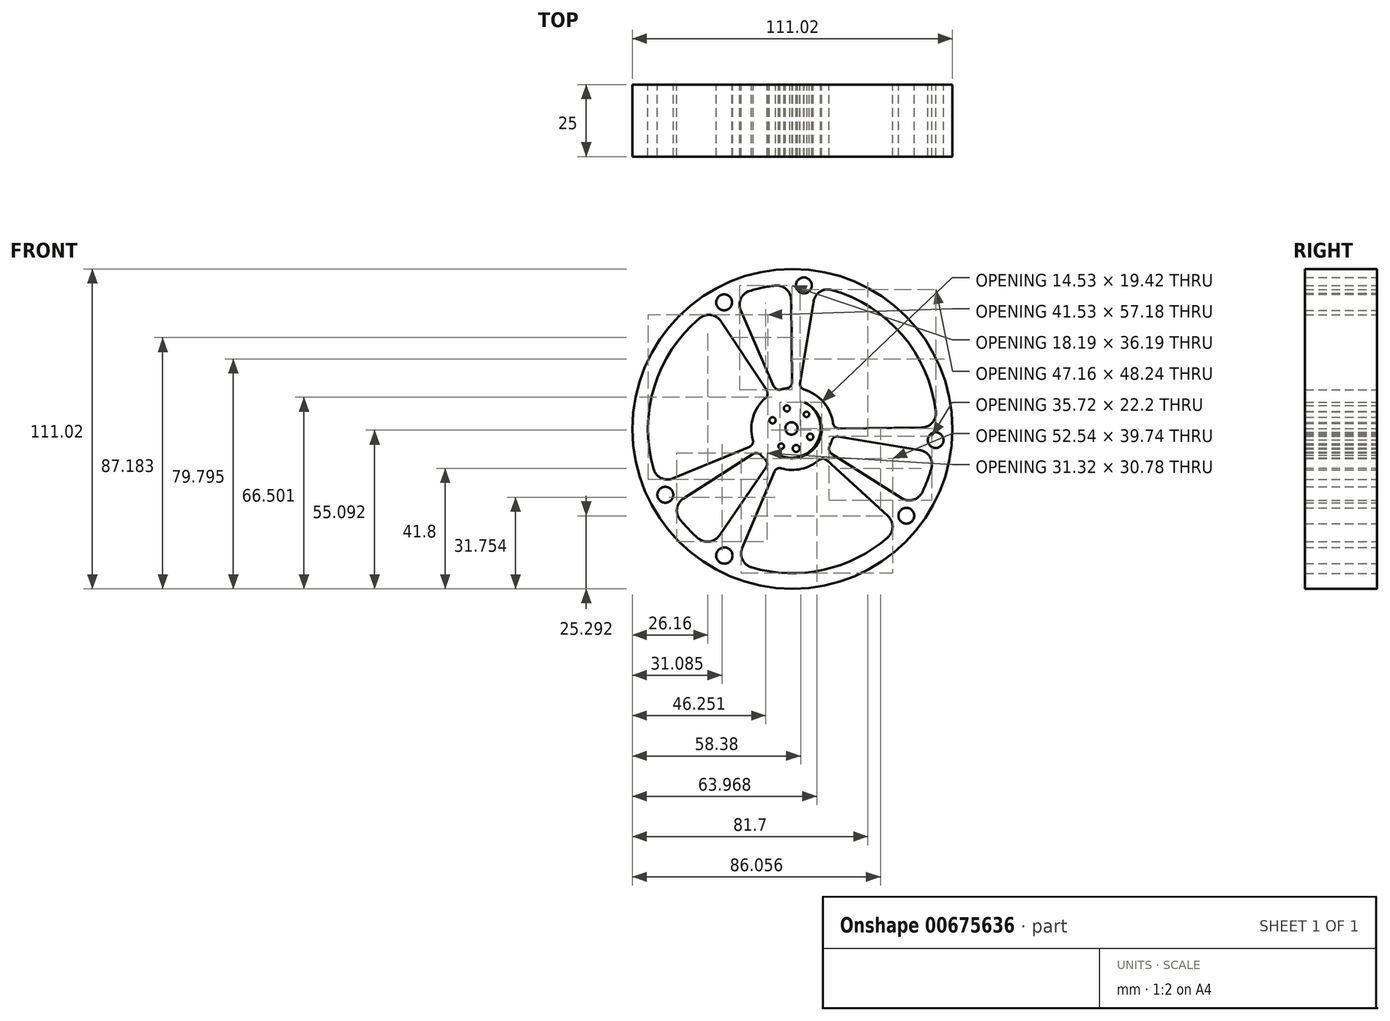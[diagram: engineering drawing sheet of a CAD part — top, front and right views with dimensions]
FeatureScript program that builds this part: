
annotation { "Feature Type Name" : "Feature", "Feature Type Description" : "" }
export const myFeature = defineFeature(function(context is Context, id is Id, definition is map)
    precondition{}
    {
        {
            var Q0;
            Q0=qCreatedBy(makeId("Front.planeOp"),FACE);
            var sketch = newSketch(context, id + "F0", { "sketchPlane" : qUnion([Q0])});
            skArc(sketch, "E0", {"start": v(-6.06, 49.75) * mm, "mid": v(-10.49, 49) * mm, "end": v(-14.83, 47.87) * mm});
            skArc(sketch, "E1", {"start": v(-9.28, 10.8) * mm, "mid": v(-13.63, 4.15) * mm, "end": v(-13.72, -3.8) * mm});
            skLineSegment(sketch, "E2", {"start": v(-0.16, 16.12) * mm, "end": v(-0.45, 44.84) * mm});
            skLineSegment(sketch, "E3", {"start": v(7.34, 44.24) * mm, "end": v(2.64, 15.9) * mm});
            skLineSegment(sketch, "E4", {"start": v(-6.45, 14.77) * mm, "end": v(-17.94, 41.1) * mm});
            skLineSegment(sketch, "E5", {"start": v(-24.8, 37.36) * mm, "end": v(-8.92, 13.43) * mm});
            skLineSegment(sketch, "E6", {"start": v(-14.88, -6.19) * mm, "end": v(-41.4, -17.22) * mm});
            skLineSegment(sketch, "E7", {"start": v(-37.78, -24.15) * mm, "end": v(-13.58, -8.68) * mm});
            skLineSegment(sketch, "E8", {"start": v(-9.11, -13.3) * mm, "end": v(-25.35, -36.99) * mm});
            skLineSegment(sketch, "E9", {"start": v(11.9, -10.87) * mm, "end": v(33.1, -30.25) * mm});
            skLineSegment(sketch, "E10", {"start": v(37.85, -24.04) * mm, "end": v(13.6, -8.64) * mm});
            skLineSegment(sketch, "E11", {"start": v(15.9, -2.64) * mm, "end": v(44.24, -7.34) * mm});
            skLineSegment(sketch, "E12", {"start": v(44.84, 0.45) * mm, "end": v(16.12, 0.16) * mm});
            skLineSegment(sketch, "E13", {"start": v(-17.42, -41.32) * mm, "end": v(-6.26, -14.85) * mm});
            skCircle(sketch, "E14", {"center": v(0, 0) * mm, "radius": 55.5 * mm});
            skArc(sketch, "E15.trimOffspring", {"start": v(49.75, 6.06) * mm, "mid": v(38.07, 32.6) * mm, "end": v(13.63, 48.23) * mm});
            skArc(sketch, "E16.trimOffspring", {"start": v(-14.23, -48.05) * mm, "mid": v(10.73, -48.96) * mm, "end": v(33.02, -37.7) * mm});
            skArc(sketch, "E17.trimOffspring", {"start": v(-38.98, -31.5) * mm, "mid": v(-36, -34.87) * mm, "end": v(-32.74, -37.95) * mm});
            skArc(sketch, "E18.trimOffspring", {"start": v(45.02, -22.02) * mm, "mid": v(46.81, -17.9) * mm, "end": v(48.23, -13.63) * mm});
            skArc(sketch, "E19.trimOffspring", {"start": v(-32.18, 38.43) * mm, "mid": v(-47.95, 14.59) * mm, "end": v(-48.12, -14) * mm});
            skCircle(sketch, "E20", {"center": v(49.69, -3.91) * mm, "radius": 2.7 * mm});
            skCircle(sketch, "E21", {"center": v(39.52, -30.16) * mm, "radius": 2.74 * mm});
            skCircle(sketch, "E22", {"center": v(-23.6, -43.97) * mm, "radius": 2.83 * mm});
            skCircle(sketch, "E23", {"center": v(-44.1, -22.9) * mm, "radius": 2.76 * mm});
            skCircle(sketch, "E24", {"center": v(-23.68, 43.91) * mm, "radius": 2.76 * mm});
            skCircle(sketch, "E25", {"center": v(3.96, 49.82) * mm, "radius": 2.75 * mm});
            skArc(sketch, "E26.trimOffspring", {"start": v(-1.9, 14.12) * mm, "mid": v(-2.98, 13.93) * mm, "end": v(-4.05, 13.66) * mm});
            skArc(sketch, "E27.trimOffspring", {"start": v(14.12, 1.9) * mm, "mid": v(10.82, 9.26) * mm, "end": v(4.04, 13.66) * mm});
            skArc(sketch, "E28.trimOffspring", {"start": v(12.87, -6.1) * mm, "mid": v(13.3, -5.09) * mm, "end": v(13.66, -4.04) * mm});
            skArc(sketch, "E29.trimOffspring", {"start": v(-3.88, -13.7) * mm, "mid": v(3.05, -13.91) * mm, "end": v(9.25, -10.83) * mm});
            skArc(sketch, "E30.trimOffspring", {"start": v(-10.97, -9.09) * mm, "mid": v(-10.23, -9.9) * mm, "end": v(-9.44, -10.67) * mm});
            skPoint(sketch, "E31.visualSharp", {"position": v(-27.72, 41.75) * mm});
            skArc(sketch, "E31.filletArc", {"start": v(-24.8, 37.36) * mm, "mid": v(-28.25, 39.54) * mm, "end": v(-32.18, 38.43) * mm});
            skPoint(sketch, "E32.visualSharp", {"position": v(-46.28, -19.24) * mm});
            skArc(sketch, "E32.filletArc", {"start": v(-48.12, -14) * mm, "mid": v(-45.48, -17.1) * mm, "end": v(-41.4, -17.22) * mm});
            skPoint(sketch, "E33.visualSharp", {"position": v(-20.05, 45.93) * mm});
            skArc(sketch, "E33.filletArc", {"start": v(-14.83, 47.87) * mm, "mid": v(-17.9, 45.18) * mm, "end": v(-17.94, 41.1) * mm});
            skPoint(sketch, "E34.visualSharp", {"position": v(-0.5, 50.12) * mm});
            skArc(sketch, "E34.filletArc", {"start": v(-0.45, 44.84) * mm, "mid": v(-2.16, 48.55) * mm, "end": v(-6.06, 49.75) * mm});
            skPoint(sketch, "E35.visualSharp", {"position": v(8.2, 49.44) * mm});
            skArc(sketch, "E35.filletArc", {"start": v(13.63, 48.23) * mm, "mid": v(9.6, 47.64) * mm, "end": v(7.34, 44.24) * mm});
            skPoint(sketch, "E36.visualSharp", {"position": v(50.12, 0.5) * mm});
            skArc(sketch, "E36.filletArc", {"start": v(44.84, 0.45) * mm, "mid": v(48.55, 2.16) * mm, "end": v(49.75, 6.06) * mm});
            skPoint(sketch, "E37.visualSharp", {"position": v(49.44, -8.2) * mm});
            skArc(sketch, "E37.filletArc", {"start": v(48.23, -13.63) * mm, "mid": v(47.64, -9.6) * mm, "end": v(44.24, -7.34) * mm});
            skPoint(sketch, "E38.visualSharp", {"position": v(42.3, -26.87) * mm});
            skArc(sketch, "E38.filletArc", {"start": v(37.85, -24.04) * mm, "mid": v(41.9, -24.63) * mm, "end": v(45.02, -22.02) * mm});
            skPoint(sketch, "E39.visualSharp", {"position": v(37, -33.8) * mm});
            skArc(sketch, "E39.filletArc", {"start": v(33.02, -37.7) * mm, "mid": v(34.73, -34) * mm, "end": v(33.1, -30.25) * mm});
            skPoint(sketch, "E40.visualSharp", {"position": v(-19.47, -46.18) * mm});
            skArc(sketch, "E40.filletArc", {"start": v(-17.42, -41.32) * mm, "mid": v(-17.33, -45.4) * mm, "end": v(-14.23, -48.05) * mm});
            skPoint(sketch, "E41.visualSharp", {"position": v(-28.33, -41.34) * mm});
            skArc(sketch, "E41.filletArc", {"start": v(-32.74, -37.95) * mm, "mid": v(-28.83, -39.12) * mm, "end": v(-25.35, -36.99) * mm});
            skPoint(sketch, "E42.visualSharp", {"position": v(-42.23, -26.99) * mm});
            skArc(sketch, "E42.filletArc", {"start": v(-37.78, -24.15) * mm, "mid": v(-40.03, -27.56) * mm, "end": v(-38.98, -31.5) * mm});
            skPoint(sketch, "E43.visualSharp", {"position": v(-12, -7.67) * mm});
            skArc(sketch, "E43.filletArc", {"start": v(-10.97, -9.09) * mm, "mid": v(-12.2, -8.39) * mm, "end": v(-13.58, -8.68) * mm});
            skPoint(sketch, "E44.visualSharp", {"position": v(-8.05, -11.75) * mm});
            skArc(sketch, "E44.filletArc", {"start": v(-9.11, -13.3) * mm, "mid": v(-8.78, -11.92) * mm, "end": v(-9.44, -10.67) * mm});
            skPoint(sketch, "E45.visualSharp", {"position": v(10.51, -9.6) * mm});
            skArc(sketch, "E45.filletArc", {"start": v(11.9, -10.87) * mm, "mid": v(10.58, -10.35) * mm, "end": v(9.25, -10.83) * mm});
            skPoint(sketch, "E46.visualSharp", {"position": v(-5.53, -13.12) * mm});
            skArc(sketch, "E46.filletArc", {"start": v(-3.88, -13.7) * mm, "mid": v(-5.29, -13.83) * mm, "end": v(-6.26, -14.85) * mm});
            skPoint(sketch, "E47.visualSharp", {"position": v(12.02, -7.64) * mm});
            skArc(sketch, "E47.filletArc", {"start": v(12.87, -6.1) * mm, "mid": v(12.76, -7.5) * mm, "end": v(13.6, -8.64) * mm});
            skPoint(sketch, "E48.visualSharp", {"position": v(14.05, -2.33) * mm});
            skArc(sketch, "E48.filletArc", {"start": v(15.9, -2.64) * mm, "mid": v(14.51, -2.92) * mm, "end": v(13.66, -4.04) * mm});
            skPoint(sketch, "E49.visualSharp", {"position": v(14.24, 0.14) * mm});
            skArc(sketch, "E49.filletArc", {"start": v(14.12, 1.9) * mm, "mid": v(14.79, 0.65) * mm, "end": v(16.12, 0.16) * mm});
            skPoint(sketch, "E50.visualSharp", {"position": v(2.33, 14.05) * mm});
            skArc(sketch, "E50.filletArc", {"start": v(2.64, 15.9) * mm, "mid": v(2.92, 14.51) * mm, "end": v(4.04, 13.66) * mm});
            skPoint(sketch, "E51.visualSharp", {"position": v(-0.14, 14.24) * mm});
            skArc(sketch, "E51.filletArc", {"start": v(-1.9, 14.12) * mm, "mid": v(-0.65, 14.79) * mm, "end": v(-0.16, 16.12) * mm});
            skPoint(sketch, "E52.visualSharp", {"position": v(-5.7, 13.05) * mm});
            skArc(sketch, "E52.filletArc", {"start": v(-6.45, 14.77) * mm, "mid": v(-5.46, 13.76) * mm, "end": v(-4.05, 13.66) * mm});
            skPoint(sketch, "E53.visualSharp", {"position": v(-7.88, 11.87) * mm});
            skArc(sketch, "E53.filletArc", {"start": v(-9.28, 10.8) * mm, "mid": v(-8.6, 12.05) * mm, "end": v(-8.92, 13.43) * mm});
            skPoint(sketch, "E54.visualSharp", {"position": v(-13.15, -5.47) * mm});
            skArc(sketch, "E54.filletArc", {"start": v(-14.88, -6.19) * mm, "mid": v(-13.85, -5.22) * mm, "end": v(-13.72, -3.8) * mm});
            skCircle(sketch, "E55", {"center": v(0, 0) * mm, "radius": 10.14 * mm});
            skPoint(sketch, "E56", {"position": v(-1.53, 6.98) * mm});
            skPoint(sketch, "E57", {"position": v(5.21, 4.88) * mm});
            skPoint(sketch, "E58", {"position": v(1.63, -6.95) * mm});
            skPoint(sketch, "E59", {"position": v(-3.56, -6.19) * mm});
            skPoint(sketch, "E60", {"position": v(-6.56, 2.81) * mm});
            skPoint(sketch, "E61", {"position": v(6.52, -2.92) * mm});
            skPoint(sketch, "E61.positionSnap0", {"position": v(14.51, -2.92) * mm});
            skCircle(sketch, "E62", {"center": v(6.52, -2.92) * mm, "radius": 1 * mm});
            skCircle(sketch, "E63", {"center": v(5.21, 4.88) * mm, "radius": 1 * mm});
            skCircle(sketch, "E64", {"center": v(-1.53, 6.98) * mm, "radius": 0.96 * mm});
            skCircle(sketch, "E65", {"center": v(-6.56, 2.81) * mm, "radius": 0.93 * mm});
            skCircle(sketch, "E66", {"center": v(-3.56, -6.19) * mm, "radius": 0.98 * mm});
            skCircle(sketch, "E67", {"center": v(1.63, -6.95) * mm, "radius": 1 * mm});
            skCircle(sketch, "E68", {"center": v(0, 0) * mm, "radius": 2.15 * mm});
            skSolve(sketch);
        }
        {
            var Q0;
            Q0 = qSketchRegion(id + "F0", true);
            extrude(context, id + "F1", {"entities" : qUnion([Q0]), "depth" : 25 * mm, "offsetDistance" : 25 * mm});
        }
        {
            var Q0;
            Q0=qCreatedBy(makeId("Front.planeOp"),FACE);
            var sketch = newSketch(context, id + "F2", { "sketchPlane" : qUnion([Q0])});
            skCircle(sketch, "E69", {"center": v(-0.33, 0.15) * mm, "radius": 10.14 * mm});
            skPoint(sketch, "E70", {"position": v(-1.86, 7.13) * mm});
            skPoint(sketch, "E71", {"position": v(4.88, 5.03) * mm});
            skPoint(sketch, "E72", {"position": v(1.3, -6.8) * mm});
            skPoint(sketch, "E73", {"position": v(-3.9, -6.04) * mm});
            skPoint(sketch, "E74", {"position": v(-6.9, 2.97) * mm});
            skPoint(sketch, "E75", {"position": v(6.19, -2.76) * mm});
            skCircle(sketch, "E76", {"center": v(-0.33, 0.15) * mm, "radius": 2.15 * mm});
            skCircle(sketch, "E77", {"center": v(-6.9, 2.97) * mm, "radius": 1.07 * mm});
            skCircle(sketch, "E78", {"center": v(-1.92, 7.1) * mm, "radius": 1.05 * mm});
            skCircle(sketch, "E79", {"center": v(4.88, 5.03) * mm, "radius": 0.93 * mm});
            skCircle(sketch, "E80", {"center": v(6.19, -2.76) * mm, "radius": 1.1 * mm});
            skCircle(sketch, "E81", {"center": v(1.3, -6.8) * mm, "radius": 1.2 * mm});
            skCircle(sketch, "E82", {"center": v(-3.9, -6.04) * mm, "radius": 0.97 * mm});
            skSolve(sketch);
        }
        {
            var Q0;
            Q0 = qSketchRegion(id + "F2", true);
            extrude(context, id + "F3", {"entities" : qUnion([Q0]), "operationType" : NewBodyOperationType.ADD, "depth" : 25 * mm, "offsetDistance" : 25 * mm});
        }
    });
